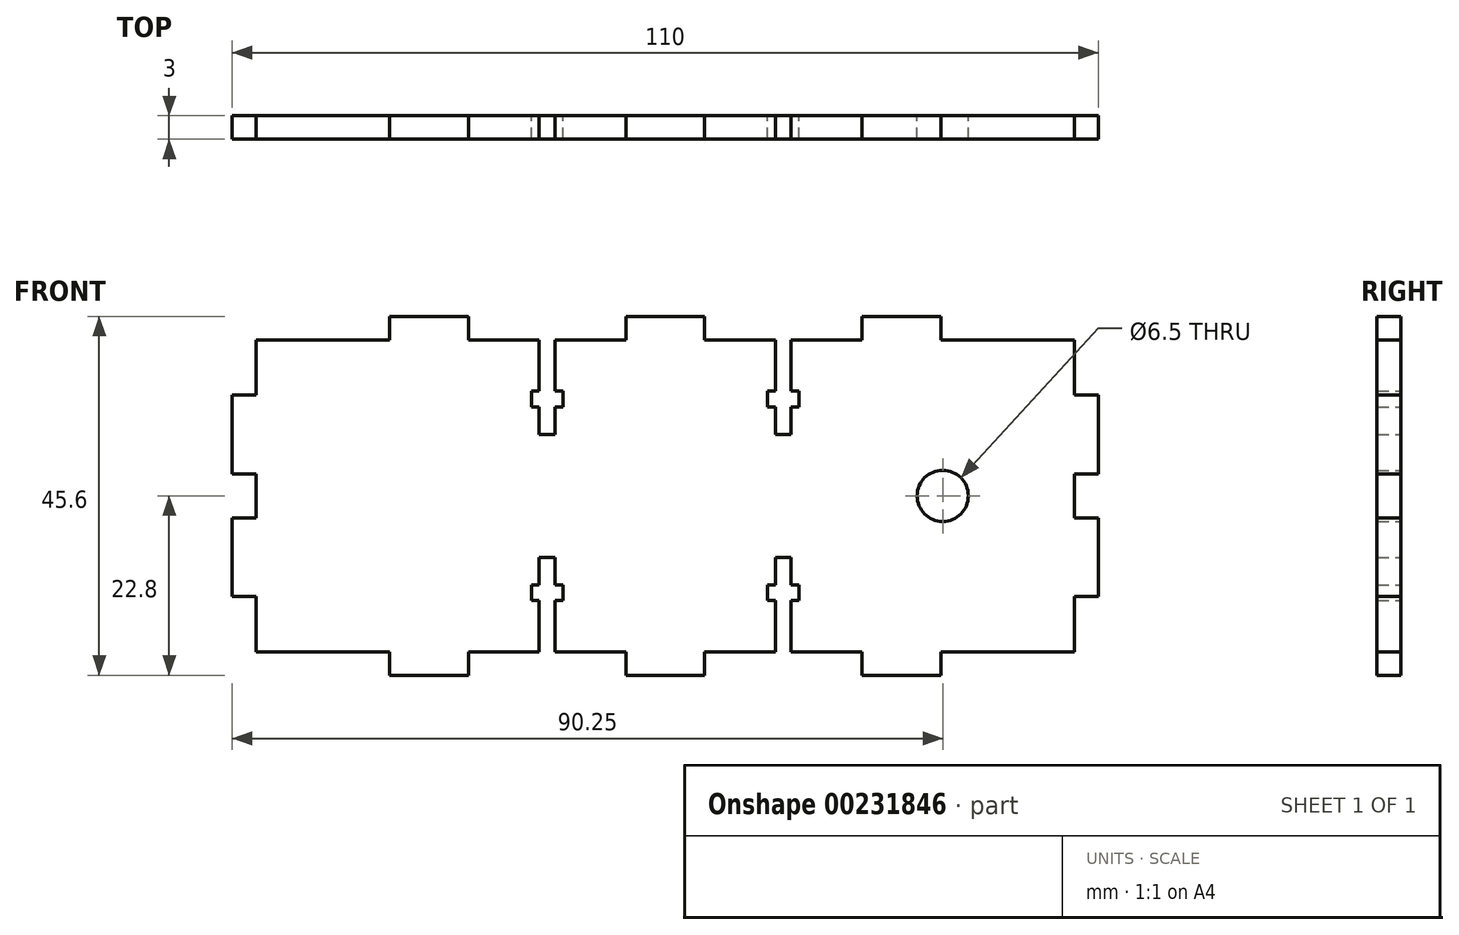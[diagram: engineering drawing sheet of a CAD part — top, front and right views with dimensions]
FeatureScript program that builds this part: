
annotation { "Feature Type Name" : "Feature", "Feature Type Description" : "" }
export const myFeature = defineFeature(function(context is Context, id is Id, definition is map)
    precondition{}
    {
        {
            var Q0;
            Q0=qCreatedBy(makeId("Front.planeOp"),FACE);
            var sketch = newSketch(context, id + "F0", { "sketchPlane" : qUnion([Q0])});
            skLineSegment(sketch, "E0", {"start": v(0, 0) * mm, "end": v(3, 0) * mm});
            skLineSegment(sketch, "E1", {"start": v(3, 0) * mm, "end": v(3, 2.8) * mm});
            skLineSegment(sketch, "E2", {"start": v(3, 2.8) * mm, "end": v(0, 2.8) * mm});
            skLineSegment(sketch, "E3", {"start": v(0, 2.8) * mm, "end": v(0, 12.8) * mm});
            skLineSegment(sketch, "E4", {"start": v(0, 12.8) * mm, "end": v(3, 12.8) * mm});
            skLineSegment(sketch, "E5", {"start": v(3, 12.8) * mm, "end": v(3, 19.8) * mm});
            skLineSegment(sketch, "E6", {"start": v(3, 19.8) * mm, "end": v(20, 19.8) * mm});
            skLineSegment(sketch, "E7", {"start": v(20, 19.8) * mm, "end": v(20, 22.8) * mm});
            skLineSegment(sketch, "E8", {"start": v(20, 22.8) * mm, "end": v(30, 22.8) * mm});
            skLineSegment(sketch, "E9", {"start": v(30, 22.8) * mm, "end": v(30, 19.8) * mm});
            skLineSegment(sketch, "E10", {"start": v(30, 19.8) * mm, "end": v(39, 19.8) * mm});
            skLineSegment(sketch, "E11", {"start": v(50, 19.8) * mm, "end": v(50, 22.8) * mm});
            skLineSegment(sketch, "E12", {"start": v(50, 22.8) * mm, "end": v(55, 22.8) * mm});
            skLineSegment(sketch, "E13", {"start": v(55, 0) * mm, "end": v(3, 0) * mm, "construction": true});
            skLineSegment(sketch, "E14.top", {"start": v(39, 7.8) * mm, "end": v(41, 7.8) * mm});
            skLineSegment(sketch, "E14.left", {"start": v(39, 19.8) * mm, "end": v(39, 13.3) * mm});
            skLineSegment(sketch, "E14.right", {"start": v(41, 19.8) * mm, "end": v(41, 13.3) * mm});
            skLineSegment(sketch, "E15", {"start": v(40, 13.3) * mm, "end": v(40, 0) * mm, "construction": true});
            skLineSegment(sketch, "E16.bottom", {"start": v(38, 13.3) * mm, "end": v(39, 13.3) * mm});
            skLineSegment(sketch, "E16.top", {"start": v(38, 11.3) * mm, "end": v(39, 11.3) * mm});
            skLineSegment(sketch, "E16.left", {"start": v(38, 13.3) * mm, "end": v(38, 11.3) * mm});
            skLineSegment(sketch, "E16.right", {"start": v(42, 13.3) * mm, "end": v(42, 11.3) * mm});
            skLineSegment(sketch, "E17.trimOffspring", {"start": v(41, 19.8) * mm, "end": v(50, 19.8) * mm});
            skPoint(sketch, "E18.orphan", {"position": v(40, 19.8) * mm});
            skLineSegment(sketch, "E19.trimOffspring", {"start": v(41, 13.3) * mm, "end": v(42, 13.3) * mm});
            skLineSegment(sketch, "E20.trimOffspring", {"start": v(41, 11.3) * mm, "end": v(42, 11.3) * mm});
            skLineSegment(sketch, "E21.trimOffspring", {"start": v(41, 11.3) * mm, "end": v(41, 7.8) * mm});
            skLineSegment(sketch, "E22.trimOffspring", {"start": v(39, 11.3) * mm, "end": v(39, 7.8) * mm});
            skLineSegment(sketch, "E23.MirrorCS", {"start": v(38, -13.3) * mm, "end": v(39, -13.3) * mm});
            skLineSegment(sketch, "E24.MirrorCS", {"start": v(41, -13.3) * mm, "end": v(42, -13.3) * mm});
            skLineSegment(sketch, "E25.MirrorCS", {"start": v(38, -11.3) * mm, "end": v(39, -11.3) * mm});
            skLineSegment(sketch, "E26.MirrorCS", {"start": v(41, -11.3) * mm, "end": v(42, -11.3) * mm});
            skLineSegment(sketch, "E27.MirrorCS", {"start": v(39, -7.8) * mm, "end": v(41, -7.8) * mm});
            skLineSegment(sketch, "E28.MirrorCS", {"start": v(3, -2.8) * mm, "end": v(0, -2.8) * mm});
            skLineSegment(sketch, "E29.MirrorCS", {"start": v(20, -19.8) * mm, "end": v(20, -22.8) * mm});
            skLineSegment(sketch, "E30.MirrorCS", {"start": v(20, -22.8) * mm, "end": v(30, -22.8) * mm});
            skLineSegment(sketch, "E31.MirrorCS", {"start": v(30, -22.8) * mm, "end": v(30, -19.8) * mm});
            skLineSegment(sketch, "E32.MirrorCS", {"start": v(41, -11.3) * mm, "end": v(41, -7.8) * mm});
            skLineSegment(sketch, "E33.MirrorCS", {"start": v(30, -19.8) * mm, "end": v(39, -19.8) * mm});
            skLineSegment(sketch, "E34.MirrorCS", {"start": v(50, -19.8) * mm, "end": v(50, -22.8) * mm});
            skLineSegment(sketch, "E35.MirrorCS", {"start": v(39, -11.3) * mm, "end": v(39, -7.8) * mm});
            skLineSegment(sketch, "E36.MirrorCS", {"start": v(50, -22.8) * mm, "end": v(55, -22.8) * mm});
            skLineSegment(sketch, "E37.MirrorCS", {"start": v(40, -13.3) * mm, "end": v(40, 0) * mm, "construction": true});
            skLineSegment(sketch, "E38.MirrorCS", {"start": v(42, -13.3) * mm, "end": v(42, -11.3) * mm});
            skLineSegment(sketch, "E39.MirrorCS", {"start": v(39, -19.8) * mm, "end": v(39, -13.3) * mm});
            skLineSegment(sketch, "E40.MirrorCS", {"start": v(3, -19.8) * mm, "end": v(20, -19.8) * mm});
            skLineSegment(sketch, "E41.MirrorCS", {"start": v(0, -12.8) * mm, "end": v(3, -12.8) * mm});
            skLineSegment(sketch, "E42.MirrorCS", {"start": v(3, 0) * mm, "end": v(3, -2.8) * mm});
            skLineSegment(sketch, "E43.MirrorCS", {"start": v(3, -12.8) * mm, "end": v(3, -19.8) * mm});
            skLineSegment(sketch, "E44.MirrorCS", {"start": v(38, -13.3) * mm, "end": v(38, -11.3) * mm});
            skLineSegment(sketch, "E45.MirrorCS", {"start": v(41, -19.8) * mm, "end": v(50, -19.8) * mm});
            skLineSegment(sketch, "E46.MirrorCS", {"start": v(41, -19.8) * mm, "end": v(41, -13.3) * mm});
            skPoint(sketch, "E47.MirrorP", {"position": v(40, -19.8) * mm});
            skLineSegment(sketch, "E48.MirrorCS", {"start": v(0, -2.8) * mm, "end": v(0, -12.8) * mm});
            skLineSegment(sketch, "E49", {"start": v(55, 22.8) * mm, "end": v(55, -22.8) * mm, "construction": true});
            skLineSegment(sketch, "E50.MirrorCS", {"start": v(69, 11.3) * mm, "end": v(68, 11.3) * mm});
            skLineSegment(sketch, "E51.MirrorCS", {"start": v(72, 11.3) * mm, "end": v(71, 11.3) * mm});
            skLineSegment(sketch, "E52.MirrorCS", {"start": v(72, -11.3) * mm, "end": v(71, -11.3) * mm});
            skLineSegment(sketch, "E53.MirrorCS", {"start": v(72, 13.3) * mm, "end": v(71, 13.3) * mm});
            skLineSegment(sketch, "E54.MirrorCS", {"start": v(69, 13.3) * mm, "end": v(68, 13.3) * mm});
            skLineSegment(sketch, "E55.MirrorCS", {"start": v(72, -13.3) * mm, "end": v(71, -13.3) * mm});
            skLineSegment(sketch, "E56.MirrorCS", {"start": v(69, -13.3) * mm, "end": v(68, -13.3) * mm});
            skLineSegment(sketch, "E57.MirrorCS", {"start": v(69, -11.3) * mm, "end": v(68, -11.3) * mm});
            skLineSegment(sketch, "E58.MirrorCS", {"start": v(68, 13.3) * mm, "end": v(68, 11.3) * mm});
            skLineSegment(sketch, "E59.MirrorCS", {"start": v(107, 2.8) * mm, "end": v(110, 2.8) * mm});
            skLineSegment(sketch, "E60.MirrorCS", {"start": v(71, 7.8) * mm, "end": v(69, 7.8) * mm});
            skLineSegment(sketch, "E61.MirrorCS", {"start": v(72, 13.3) * mm, "end": v(72, 11.3) * mm});
            skLineSegment(sketch, "E62.MirrorCS", {"start": v(71, -7.8) * mm, "end": v(69, -7.8) * mm});
            skLineSegment(sketch, "E63.MirrorCS", {"start": v(60, -19.8) * mm, "end": v(60, -22.8) * mm});
            skPoint(sketch, "E64.MirrorP", {"position": v(70, 19.8) * mm});
            skLineSegment(sketch, "E65.MirrorCS", {"start": v(107, 19.8) * mm, "end": v(90, 19.8) * mm});
            skLineSegment(sketch, "E66.MirrorCS", {"start": v(68, -13.3) * mm, "end": v(68, -11.3) * mm});
            skLineSegment(sketch, "E67.MirrorCS", {"start": v(69, 19.8) * mm, "end": v(69, 13.3) * mm});
            skLineSegment(sketch, "E68.MirrorCS", {"start": v(70, -13.3) * mm, "end": v(70, 0) * mm, "construction": true});
            skLineSegment(sketch, "E69.MirrorCS", {"start": v(71, 19.8) * mm, "end": v(71, 13.3) * mm});
            skLineSegment(sketch, "E70.MirrorCS", {"start": v(72, -13.3) * mm, "end": v(72, -11.3) * mm});
            skLineSegment(sketch, "E71.MirrorCS", {"start": v(69, 11.3) * mm, "end": v(69, 7.8) * mm});
            skLineSegment(sketch, "E72.MirrorCS", {"start": v(69, 19.8) * mm, "end": v(60, 19.8) * mm});
            skLineSegment(sketch, "E73.MirrorCS", {"start": v(80, 19.8) * mm, "end": v(71, 19.8) * mm});
            skLineSegment(sketch, "E74.MirrorCS", {"start": v(80, 22.8) * mm, "end": v(80, 19.8) * mm});
            skLineSegment(sketch, "E75.MirrorCS", {"start": v(110, 2.8) * mm, "end": v(110, 12.8) * mm});
            skLineSegment(sketch, "E76.MirrorCS", {"start": v(107, -12.8) * mm, "end": v(107, -19.8) * mm});
            skLineSegment(sketch, "E77.MirrorCS", {"start": v(107, -2.8) * mm, "end": v(110, -2.8) * mm});
            skLineSegment(sketch, "E78.MirrorCS", {"start": v(71, -19.8) * mm, "end": v(71, -13.3) * mm});
            skLineSegment(sketch, "E79.MirrorCS", {"start": v(80, -22.8) * mm, "end": v(80, -19.8) * mm});
            skLineSegment(sketch, "E80.MirrorCS", {"start": v(107, -19.8) * mm, "end": v(90, -19.8) * mm});
            skLineSegment(sketch, "E81.MirrorCS", {"start": v(107, 0) * mm, "end": v(107, 2.8) * mm});
            skLineSegment(sketch, "E82.MirrorCS", {"start": v(90, -22.8) * mm, "end": v(80, -22.8) * mm});
            skLineSegment(sketch, "E83.MirrorCS", {"start": v(69, -19.8) * mm, "end": v(60, -19.8) * mm});
            skLineSegment(sketch, "E84.MirrorCS", {"start": v(71, 11.3) * mm, "end": v(71, 7.8) * mm});
            skLineSegment(sketch, "E85.MirrorCS", {"start": v(107, 0) * mm, "end": v(107, -2.8) * mm});
            skLineSegment(sketch, "E86.MirrorCS", {"start": v(90, -19.8) * mm, "end": v(90, -22.8) * mm});
            skLineSegment(sketch, "E87.MirrorCS", {"start": v(90, 19.8) * mm, "end": v(90, 22.8) * mm});
            skLineSegment(sketch, "E88.MirrorCS", {"start": v(110, 12.8) * mm, "end": v(107, 12.8) * mm});
            skLineSegment(sketch, "E89.MirrorCS", {"start": v(110, -12.8) * mm, "end": v(107, -12.8) * mm});
            skPoint(sketch, "E90.MirrorP", {"position": v(70, -19.8) * mm});
            skLineSegment(sketch, "E91.MirrorCS", {"start": v(71, -11.3) * mm, "end": v(71, -7.8) * mm});
            skLineSegment(sketch, "E92.MirrorCS", {"start": v(69, -19.8) * mm, "end": v(69, -13.3) * mm});
            skLineSegment(sketch, "E93.MirrorCS", {"start": v(60, 19.8) * mm, "end": v(60, 22.8) * mm});
            skLineSegment(sketch, "E94.MirrorCS", {"start": v(80, -19.8) * mm, "end": v(71, -19.8) * mm});
            skLineSegment(sketch, "E95.MirrorCS", {"start": v(69, -11.3) * mm, "end": v(69, -7.8) * mm});
            skLineSegment(sketch, "E96.MirrorCS", {"start": v(110, -2.8) * mm, "end": v(110, -12.8) * mm});
            skLineSegment(sketch, "E97.MirrorCS", {"start": v(70, 13.3) * mm, "end": v(70, 0) * mm, "construction": true});
            skLineSegment(sketch, "E98.MirrorCS", {"start": v(90, 22.8) * mm, "end": v(80, 22.8) * mm});
            skLineSegment(sketch, "E99.MirrorCS", {"start": v(107, 12.8) * mm, "end": v(107, 19.8) * mm});
            skLineSegment(sketch, "E100", {"start": v(55, 22.8) * mm, "end": v(60, 22.8) * mm});
            skLineSegment(sketch, "E101", {"start": v(55, -22.8) * mm, "end": v(60, -22.8) * mm});
            skLineSegment(sketch, "E102", {"start": v(55, 0) * mm, "end": v(107, 0) * mm, "construction": true});
            skPoint(sketch, "E103.MirrorCS.start.orphan", {"position": v(110, 0) * mm});
            skCircle(sketch, "E104", {"center": v(90.25, 0) * mm, "radius": 3.25 * mm});
            skSolve(sketch);
        }
        {
            var Q0;
            Q0=makeQuery(id+"F0.imprint","IMPRINT",FACE,{"disambiguationData":[TD([[makeQuery(id+"F0.imprint","IMPRINT",EDGE,{"derivedFrom":sQuery(id+"F0.wireOp",EDGE,"E1")}),-1.0]])]});
            extrude(context, id + "F1", {"entities" : qUnion([Q0]), "depth" : 3 * mm});
        }
    });
